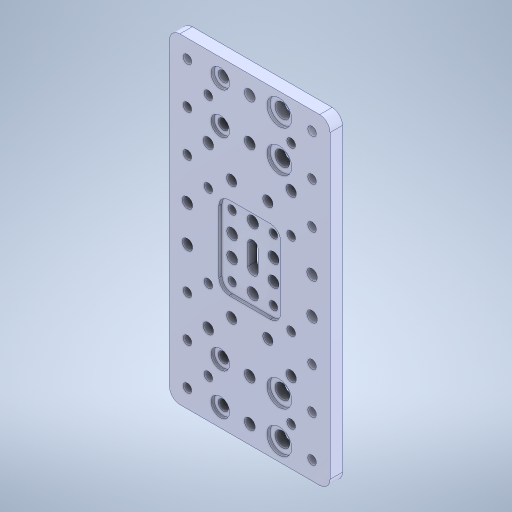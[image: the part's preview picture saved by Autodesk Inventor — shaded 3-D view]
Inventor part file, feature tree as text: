
AUTODESK INVENTOR PART (.ipt)
format: ipt  version: 2024.3 (Build 283343000, 343)  size: 365,056 bytes
history: native  units: in
note: dims shown in document units (in); Inventor stores cm internally (conversion verified against a paired STEP export)
features: mirror x1
ambient origin geometry x8: Origin, YZ Plane, XZ Plane, XY Plane, X Axis, Y Axis, Z Axis, Center Point
bodies: Solid1 (feature_tree)
feature tree (1):
  mirror  "Mirror1"
